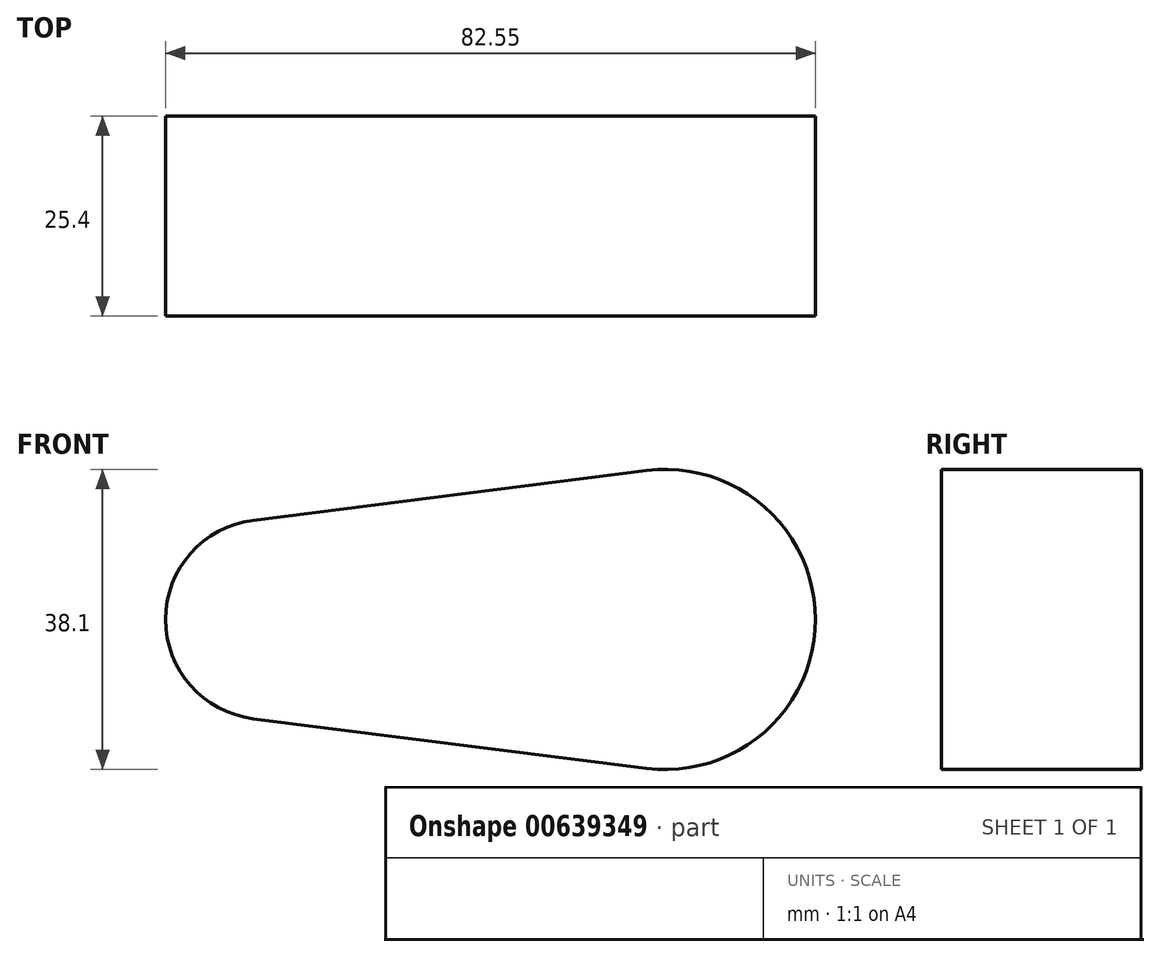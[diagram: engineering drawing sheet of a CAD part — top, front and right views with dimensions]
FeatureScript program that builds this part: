
annotation { "Feature Type Name" : "Feature", "Feature Type Description" : "" }
export const myFeature = defineFeature(function(context is Context, id is Id, definition is map)
    precondition{}
    {
        {
            var Q0;
            Q0=qCreatedBy(makeId("Front.planeOp"),FACE);
            var sketch = newSketch(context, id + "F0", { "sketchPlane" : qUnion([Q0])});
            skCircle(sketch, "E0", {"center": v(-28.92, 0) * mm, "radius": 12.7 * mm});
            skCircle(sketch, "E1", {"center": v(21.88, 0) * mm, "radius": 19.05 * mm});
            skLineSegment(sketch, "E2", {"start": v(-28.92, 0) * mm, "end": v(21.88, 0) * mm});
            skLineSegment(sketch, "E3", {"start": v(-30.51, 12.6) * mm, "end": v(19.5, 18.9) * mm});
            skLineSegment(sketch, "E4", {"start": v(-25.39, -25.2) * mm, "end": v(19.5, -18.9) * mm});
            skLineSegment(sketch, "E5", {"start": v(21.88, 0) * mm, "end": v(19.5, -18.9) * mm});
            skLineSegment(sketch, "E6", {"start": v(21.88, 0) * mm, "end": v(19.5, 18.9) * mm});
            skLineSegment(sketch, "E7", {"start": v(-25.39, -25.2) * mm, "end": v(-28.92, 0) * mm});
            skLineSegment(sketch, "E8", {"start": v(-28.92, 0) * mm, "end": v(-30.51, 12.6) * mm});
            skLineSegment(sketch, "E9", {"start": v(-13.82, 58.83) * mm, "end": v(18.57, 69.85) * mm});
            skLineSegment(sketch, "E10", {"start": v(-30.51, -12.6) * mm, "end": v(19.5, -18.9) * mm});
            skPoint(sketch, "E10.startSnap0", {"position": v(-27.16, -12.6) * mm});
            skLineSegment(sketch, "E11", {"start": v(-30.51, -12.6) * mm, "end": v(-28.92, 0) * mm});
            skSolve(sketch);
        }
        {
            var Q0;
            {var subQ3=sQuery(id+"F0.wireOp",EDGE,"E0");var subQ7=sQuery(id+"F0.wireOp",EDGE,"E2");var subQ9=makeQuery(id+"F0.imprint","INTERSECT",VERTEX,{"derivedFrom":[subQ3,subQ7]});Q0=makeQuery(id+"F0.imprint","IMPRINT",FACE,{"disambiguationData":[TD([[makeQuery(id+"F0.imprint","IMPRINT",EDGE,{"disambiguationData":[TD([[subQ9,1.0]])],"derivedFrom":subQ3}),-1.0]])]});}
            var Q1;
            {var subQ0=sQuery(id+"F0.wireOp",EDGE,"E2");var subQ1=sQuery(id+"F0.wireOp",EDGE,"E0");var subQ2=makeQuery(id+"F0.imprint","INTERSECT",VERTEX,{"derivedFrom":[subQ1,subQ0]});Q1=makeQuery(id+"F0.imprint","IMPRINT",FACE,{"disambiguationData":[TD([[makeQuery(id+"F0.imprint","IMPRINT",EDGE,{"disambiguationData":[TD([[subQ2,1.0]])],"derivedFrom":subQ1}),1.0]])]});}
            var Q2;
            {var subQ0=sQuery(id+"F0.wireOp",EDGE,"E5");Q2=makeQuery(id+"F0.imprint","IMPRINT",FACE,{"disambiguationData":[TD([[makeQuery(id+"F0.imprint","IMPRINT",EDGE,{"derivedFrom":subQ0}),-1.0]])]});}
            var Q3;
            {var subQ2=sQuery(id+"F0.wireOp",EDGE,"E5");Q3=makeQuery(id+"F0.imprint","IMPRINT",FACE,{"disambiguationData":[TD([[makeQuery(id+"F0.imprint","IMPRINT",EDGE,{"derivedFrom":subQ2}),1.0]])]});}
            var Q4;
            {var subQ0=sQuery(id+"F0.wireOp",EDGE,"E6");Q4=makeQuery(id+"F0.imprint","IMPRINT",FACE,{"disambiguationData":[TD([[makeQuery(id+"F0.imprint","IMPRINT",EDGE,{"derivedFrom":subQ0}),1.0]])]});}
            var Q5;
            {var subQ0=sQuery(id+"F0.wireOp",EDGE,"E3");Q5=makeQuery(id+"F0.imprint","IMPRINT",FACE,{"disambiguationData":[TD([[makeQuery(id+"F0.imprint","IMPRINT",EDGE,{"derivedFrom":subQ0}),-1.0]])]});}
            var Q6;
            {var subQ0=sQuery(id+"F0.wireOp",EDGE,"E11");Q6=makeQuery(id+"F0.imprint","IMPRINT",FACE,{"disambiguationData":[TD([[makeQuery(id+"F0.imprint","IMPRINT",EDGE,{"derivedFrom":subQ0}),-1.0]])]});}
            var Q7;
            {var subQ0=sQuery(id+"F0.wireOp",EDGE,"E8");Q7=makeQuery(id+"F0.imprint","IMPRINT",FACE,{"disambiguationData":[TD([[makeQuery(id+"F0.imprint","IMPRINT",EDGE,{"derivedFrom":subQ0}),-1.0]])]});}
            var Q8;
            {var subQ0=sQuery(id+"F0.wireOp",EDGE,"E8");Q8=makeQuery(id+"F0.imprint","IMPRINT",FACE,{"disambiguationData":[TD([[makeQuery(id+"F0.imprint","IMPRINT",EDGE,{"derivedFrom":subQ0}),1.0]])]});}
            var Q9;
            {var subQ0=sQuery(id+"F0.wireOp",EDGE,"E10");var subQ3=sQuery(id+"F0.wireOp",EDGE,"E7");var subQ5=makeQuery(id+"F0.imprint","INTERSECT",VERTEX,{"derivedFrom":[subQ3,subQ0]});Q9=makeQuery(id+"F0.imprint","IMPRINT",FACE,{"disambiguationData":[TD([[makeQuery(id+"F0.imprint","IMPRINT",EDGE,{"disambiguationData":[TD([[subQ5,-1.0]])],"derivedFrom":subQ3}),1.0]])]});}
            extrude(context, id + "F1", {"entities" : qUnion([Q0, Q1, Q2, Q3, Q4, Q5, Q6, Q7, Q8, Q9]), "depth" : 25.4 * mm, "offsetDistance" : 25.4 * mm});
        }
    });
